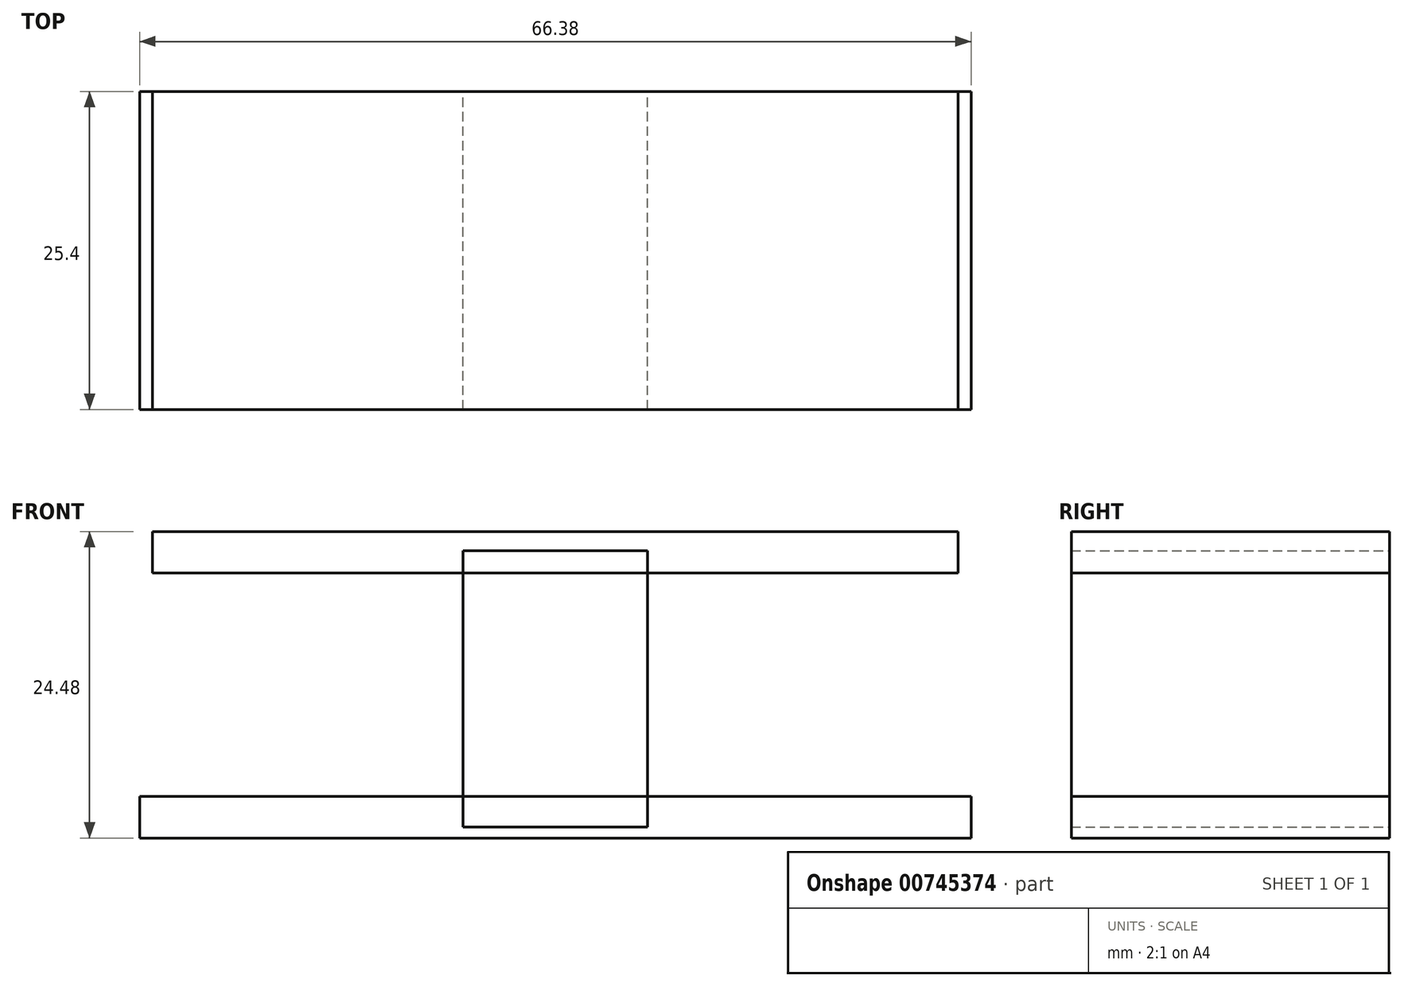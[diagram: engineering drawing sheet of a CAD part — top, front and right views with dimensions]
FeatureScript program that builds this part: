
annotation { "Feature Type Name" : "Feature", "Feature Type Description" : "" }
export const myFeature = defineFeature(function(context is Context, id is Id, definition is map)
    precondition{}
    {
        {
            var Q0;
            Q0=qCreatedBy(makeId("Front.planeOp"),FACE);
            var sketch = newSketch(context, id + "F0", { "sketchPlane" : qUnion([Q0])});
            skLineSegment(sketch, "E0.bottom", {"start": v(33.2, 22) * mm, "end": v(-33.2, 22) * mm});
            skLineSegment(sketch, "E0.top", {"start": v(33.2, 18.67) * mm, "end": v(-33.2, 18.67) * mm});
            skLineSegment(sketch, "E0.left", {"start": v(33.2, 22) * mm, "end": v(33.2, 18.67) * mm});
            skLineSegment(sketch, "E0.right", {"start": v(-33.2, 22) * mm, "end": v(-33.2, 18.67) * mm});
            skPoint(sketch, "E0.middle", {"position": v(0, 20.33) * mm});
            skLineSegment(sketch, "E1.bottom", {"start": v(-32.16, 43.15) * mm, "end": v(32.16, 43.15) * mm});
            skLineSegment(sketch, "E1.top", {"start": v(-32.16, 39.83) * mm, "end": v(32.16, 39.83) * mm});
            skLineSegment(sketch, "E1.left", {"start": v(-32.16, 43.15) * mm, "end": v(-32.16, 39.83) * mm});
            skLineSegment(sketch, "E1.right", {"start": v(32.16, 43.15) * mm, "end": v(32.16, 39.83) * mm});
            skPoint(sketch, "E1.middle", {"position": v(0, 41.5) * mm});
            skSolve(sketch);
        }
        {
            var Q0;
            Q0 = qSketchRegion(id + "F0", true);
            extrude(context, id + "F1", {"entities" : qUnion([Q0]), "depth" : 25.4 * mm, "offsetDistance" : 25.4 * mm});
        }
        {
            var Q0;
            Q0=qCreatedBy(makeId("Front.planeOp"),FACE);
            var sketch = newSketch(context, id + "F2", { "sketchPlane" : qUnion([Q0])});
            skLineSegment(sketch, "E2.bottom", {"start": v(7.37, 19.56) * mm, "end": v(-7.37, 19.56) * mm});
            skLineSegment(sketch, "E2.top", {"start": v(7.37, 41.6) * mm, "end": v(-7.37, 41.6) * mm});
            skLineSegment(sketch, "E2.left", {"start": v(7.37, 19.56) * mm, "end": v(7.37, 41.6) * mm});
            skLineSegment(sketch, "E2.right", {"start": v(-7.37, 19.56) * mm, "end": v(-7.37, 41.6) * mm});
            skPoint(sketch, "E2.middle", {"position": v(0, 30.58) * mm});
            skSolve(sketch);
        }
        {
            var Q0;
            Q0 = qSketchRegion(id + "F2", true);
            extrude(context, id + "F3", {"entities" : qUnion([Q0]), "depth" : 25.4 * mm, "offsetDistance" : 25.4 * mm});
        }
    });
